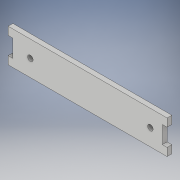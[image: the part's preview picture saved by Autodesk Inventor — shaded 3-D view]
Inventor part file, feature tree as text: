
AUTODESK INVENTOR PART (.ipt)
format: ipt  version: 2019 (Build 230136000, 136)  size: 118,784 bytes
history: native  units: mm
features: extrude x1, sketch x1
ambient origin geometry x8: Origin, YZ Plane, XZ Plane, XY Plane, X Axis, Y Axis, Z Axis, Center Point
bodies: Body1 (feature_tree)
feature tree (2):
  extrude  "Extrusion3"  Depth=6.0mm
  sketch  "Sketch1"  dims[d31=200.0mm d35=6.0mm d36=10.0mm d37=10.0mm d38=23.0mm d39=10.0mm d40=10.0mm d41=6.0mm d42=7.0mm d43=15.0mm d44=21.0mm d45=42.0mm d46=10.0mm d47=7.0mm d48=21.0mm d49=28.0mm d50=6.0mm d51=0.0mm]
